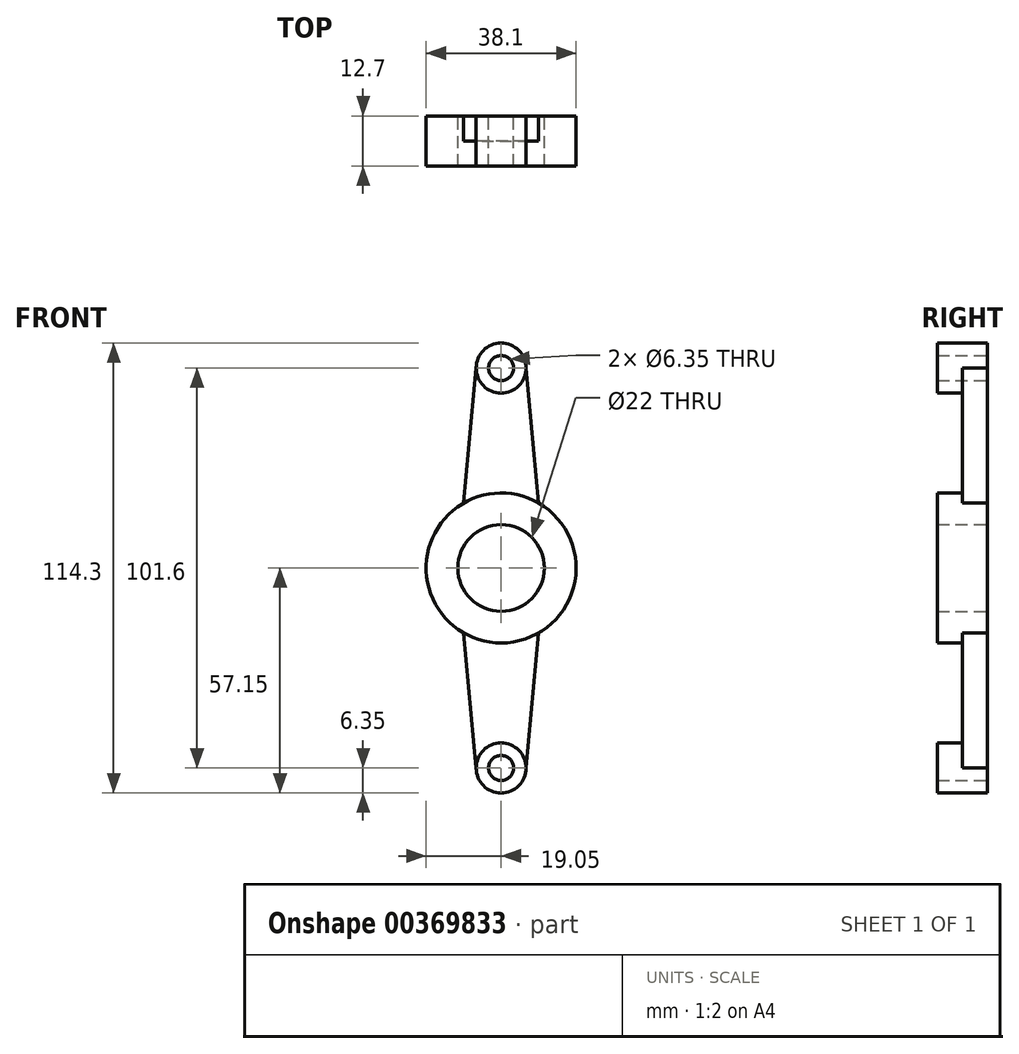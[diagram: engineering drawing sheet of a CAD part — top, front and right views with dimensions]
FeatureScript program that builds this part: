
annotation { "Feature Type Name" : "Feature", "Feature Type Description" : "" }
export const myFeature = defineFeature(function(context is Context, id is Id, definition is map)
    precondition{}
    {
        {
            var Q0;
            Q0=qCreatedBy(makeId("Front.planeOp"),FACE);
            var sketch = newSketch(context, id + "F0", { "sketchPlane" : qUnion([Q0])});
            skCircle(sketch, "E0", {"center": v(0, 0) * mm, "radius": 19.05 * mm});
            skCircle(sketch, "E1", {"center": v(0, 0) * mm, "radius": 11 * mm});
            skCircle(sketch, "E2", {"center": v(0, 50.8) * mm, "radius": 6.35 * mm});
            skCircle(sketch, "E3", {"center": v(0, 50.8) * mm, "radius": 3.18 * mm});
            skCircle(sketch, "E4", {"center": v(0, -50.8) * mm, "radius": 6.35 * mm});
            skCircle(sketch, "E5", {"center": v(0, -50.8) * mm, "radius": 3.18 * mm});
            skLineSegment(sketch, "E6", {"start": v(-6.35, 50.8) * mm, "end": v(-9.52, 16.5) * mm});
            skLineSegment(sketch, "E7", {"start": v(6.35, 50.8) * mm, "end": v(9.52, 16.5) * mm});
            skLineSegment(sketch, "E8", {"start": v(-6.35, -50.8) * mm, "end": v(-9.52, -16.5) * mm});
            skLineSegment(sketch, "E9", {"start": v(6.35, -50.8) * mm, "end": v(9.52, -16.5) * mm});
            skSolve(sketch);
        }
        {
            var Q0;
            Q0 = qSketchRegion(id + "F0", true);
            extrude(context, id + "F1", {"entities" : qUnion([Q0]), "depth" : 6.35 * mm});
        }
        {
            var Q0;
            Q0=makeQuery(id+"F0.imprint","IMPRINT",FACE,{"disambiguationData":[TD([[makeQuery(id+"F0.imprint","IMPRINT",EDGE,{"derivedFrom":sQuery(id+"F0.wireOp",EDGE,"E3")}),-1.0]])]});
            var Q1;
            Q1=makeQuery(id+"F0.imprint","IMPRINT",FACE,{"disambiguationData":[TD([[makeQuery(id+"F0.imprint","IMPRINT",EDGE,{"derivedFrom":sQuery(id+"F0.wireOp",EDGE,"E1")}),-1.0]])]});
            var Q2;
            Q2=makeQuery(id+"F0.imprint","IMPRINT",FACE,{"disambiguationData":[TD([[makeQuery(id+"F0.imprint","IMPRINT",EDGE,{"derivedFrom":sQuery(id+"F0.wireOp",EDGE,"E5")}),-1.0]])]});
            extrude(context, id + "F2", {"entities" : qUnion([Q0, Q1, Q2]), "operationType" : NewBodyOperationType.ADD, "depth" : 12.7 * mm});
        }
    });
